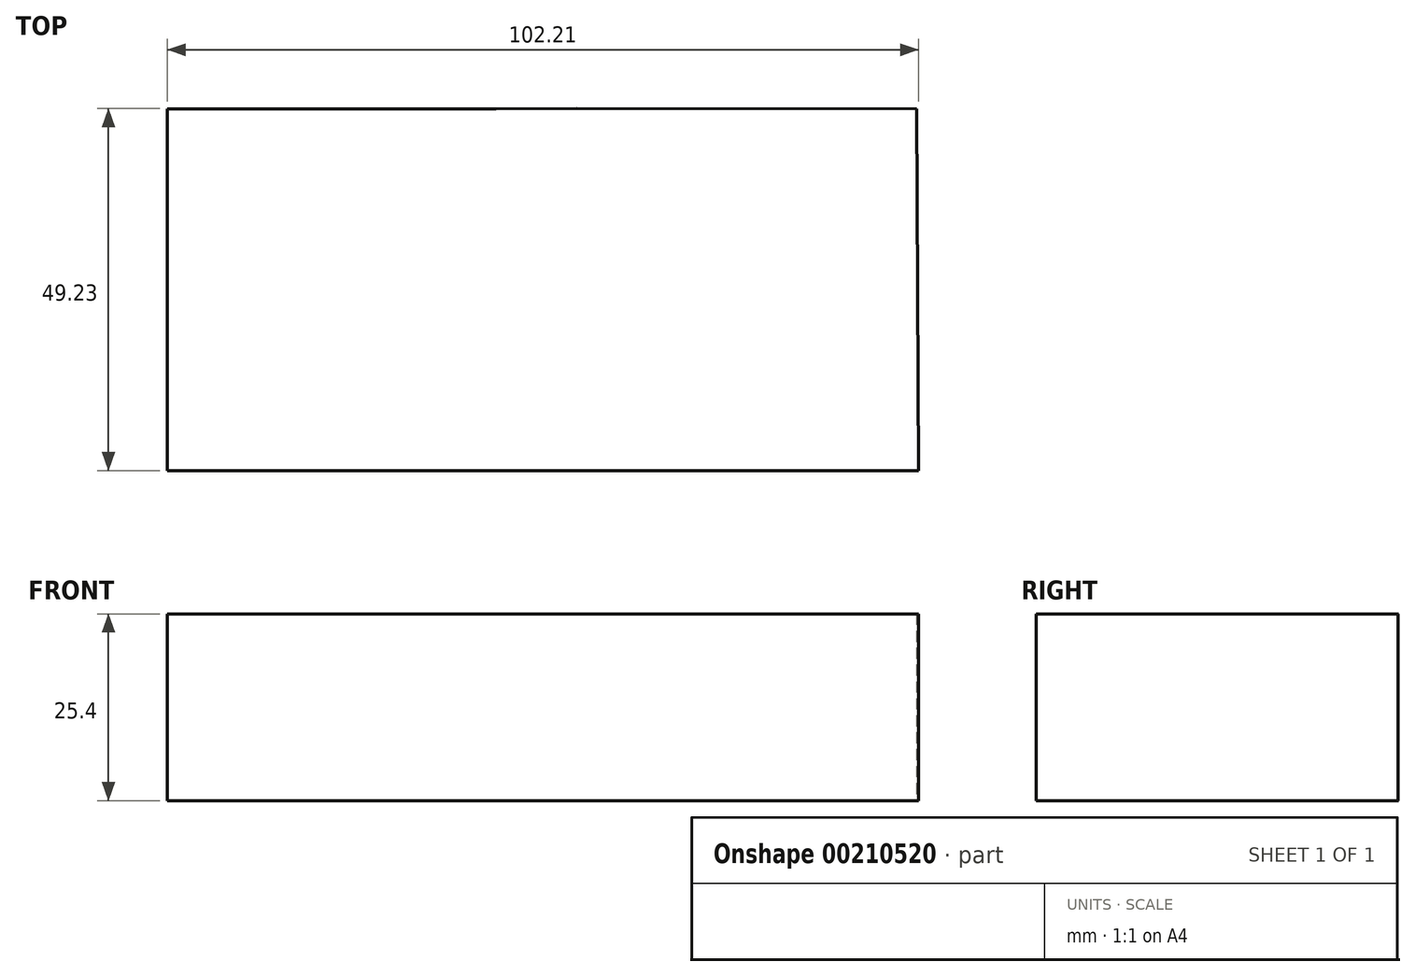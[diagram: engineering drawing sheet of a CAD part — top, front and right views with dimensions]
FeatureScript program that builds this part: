
annotation { "Feature Type Name" : "Feature", "Feature Type Description" : "" }
export const myFeature = defineFeature(function(context is Context, id is Id, definition is map)
    precondition{}
    {
        {
            var Q0;
            Q0=qCreatedBy(makeId("Top.planeOp"),FACE);
            var sketch = newSketch(context, id + "F0", { "sketchPlane" : qUnion([Q0])});
            skLineSegment(sketch, "E0", {"start": v(-5.66, 18.33) * mm, "end": v(-50.36, 18.33) * mm});
            skLineSegment(sketch, "E1", {"start": v(-50.36, 18.33) * mm, "end": v(-50.36, -30.84) * mm});
            skLineSegment(sketch, "E2", {"start": v(-50.36, -30.84) * mm, "end": v(-5.36, -30.84) * mm});
            skLineSegment(sketch, "E3", {"start": v(-5.66, 18.33) * mm, "end": v(-5.36, -30.84) * mm});
            skLineSegment(sketch, "E4", {"start": v(-5.66, 18.33) * mm, "end": v(5.36, 18.4) * mm});
            skLineSegment(sketch, "E5", {"start": v(5.36, 18.4) * mm, "end": v(5.66, -30.84) * mm});
            skLineSegment(sketch, "E6", {"start": v(5.66, -30.84) * mm, "end": v(-5.36, -30.84) * mm});
            skLineSegment(sketch, "E7", {"start": v(5.36, 18.4) * mm, "end": v(51.55, 18.33) * mm});
            skLineSegment(sketch, "E8", {"start": v(51.55, 18.33) * mm, "end": v(51.85, -30.84) * mm});
            skLineSegment(sketch, "E9", {"start": v(5.66, -30.84) * mm, "end": v(51.85, -30.84) * mm});
            skSolve(sketch);
        }
        {
            var Q0;
            Q0=makeQuery(id+"F0.imprint","IMPRINT",FACE,{"disambiguationData":[TD([[makeQuery(id+"F0.imprint","IMPRINT",EDGE,{"derivedFrom":sQuery(id+"F0.wireOp",EDGE,"E0")}),1.0]])]});
            var Q1;
            Q1=makeQuery(id+"F0.imprint","IMPRINT",FACE,{"disambiguationData":[TD([[makeQuery(id+"F0.imprint","IMPRINT",EDGE,{"derivedFrom":sQuery(id+"F0.wireOp",EDGE,"E3")}),1.0]])]});
            var Q2;
            Q2=makeQuery(id+"F0.imprint","IMPRINT",FACE,{"disambiguationData":[TD([[makeQuery(id+"F0.imprint","IMPRINT",EDGE,{"derivedFrom":sQuery(id+"F0.wireOp",EDGE,"E5")}),1.0]])]});
            extrude(context, id + "F1", {"entities" : qUnion([Q0, Q1, Q2]), "depth" : 25.4 * mm});
        }
    });
